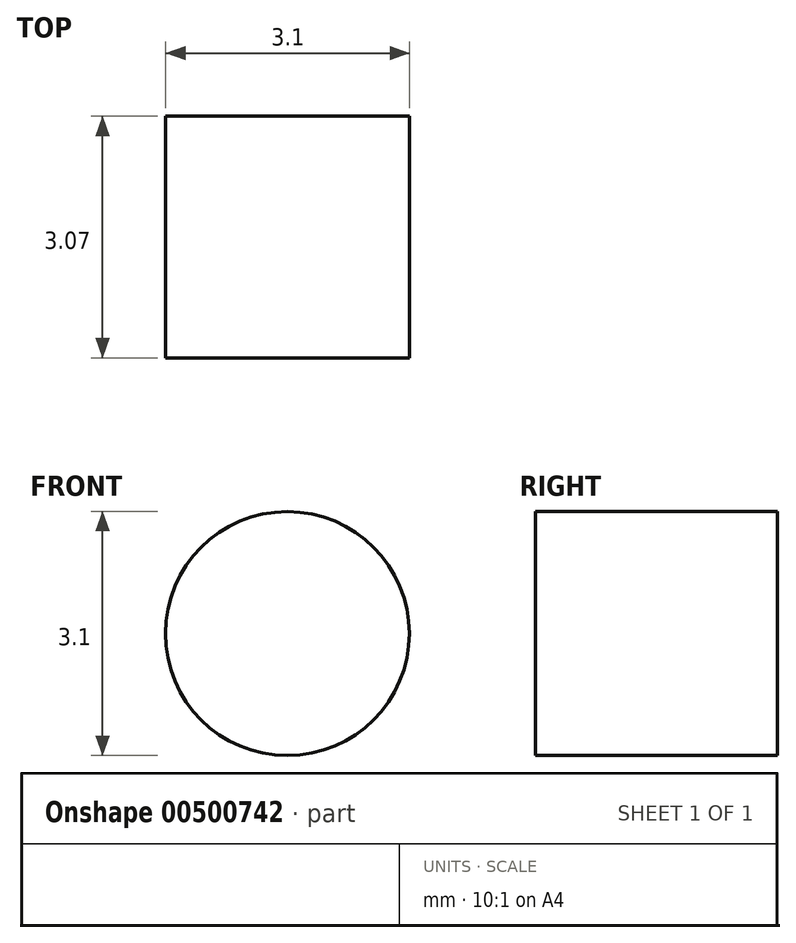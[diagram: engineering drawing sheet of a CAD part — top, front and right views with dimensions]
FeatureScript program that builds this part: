
annotation { "Feature Type Name" : "Feature", "Feature Type Description" : "" }
export const myFeature = defineFeature(function(context is Context, id is Id, definition is map)
    precondition{}
    {
        {
            var Q0;
            Q0=qCreatedBy(makeId("Front.planeOp"),FACE);
            var sketch = newSketch(context, id + "F0", { "sketchPlane" : qUnion([Q0])});
            skCircle(sketch, "E0", {"center": v(-45.81, 21.82) * mm, "radius": 1.55 * mm});
            skSolve(sketch);
        }
        {
            var Q0;
            Q0=makeQuery(id+"F0.imprint","IMPRINT",FACE,{"disambiguationData":[TD([[makeQuery(id+"F0.imprint","IMPRINT",EDGE,{"derivedFrom":sQuery(id+"F0.wireOp",EDGE,"E0")}),1.0]])]});
            extrude(context, id + "F1", {"entities" : qUnion([Q0]), "depth" : 3.07 * mm});
        }
    });
